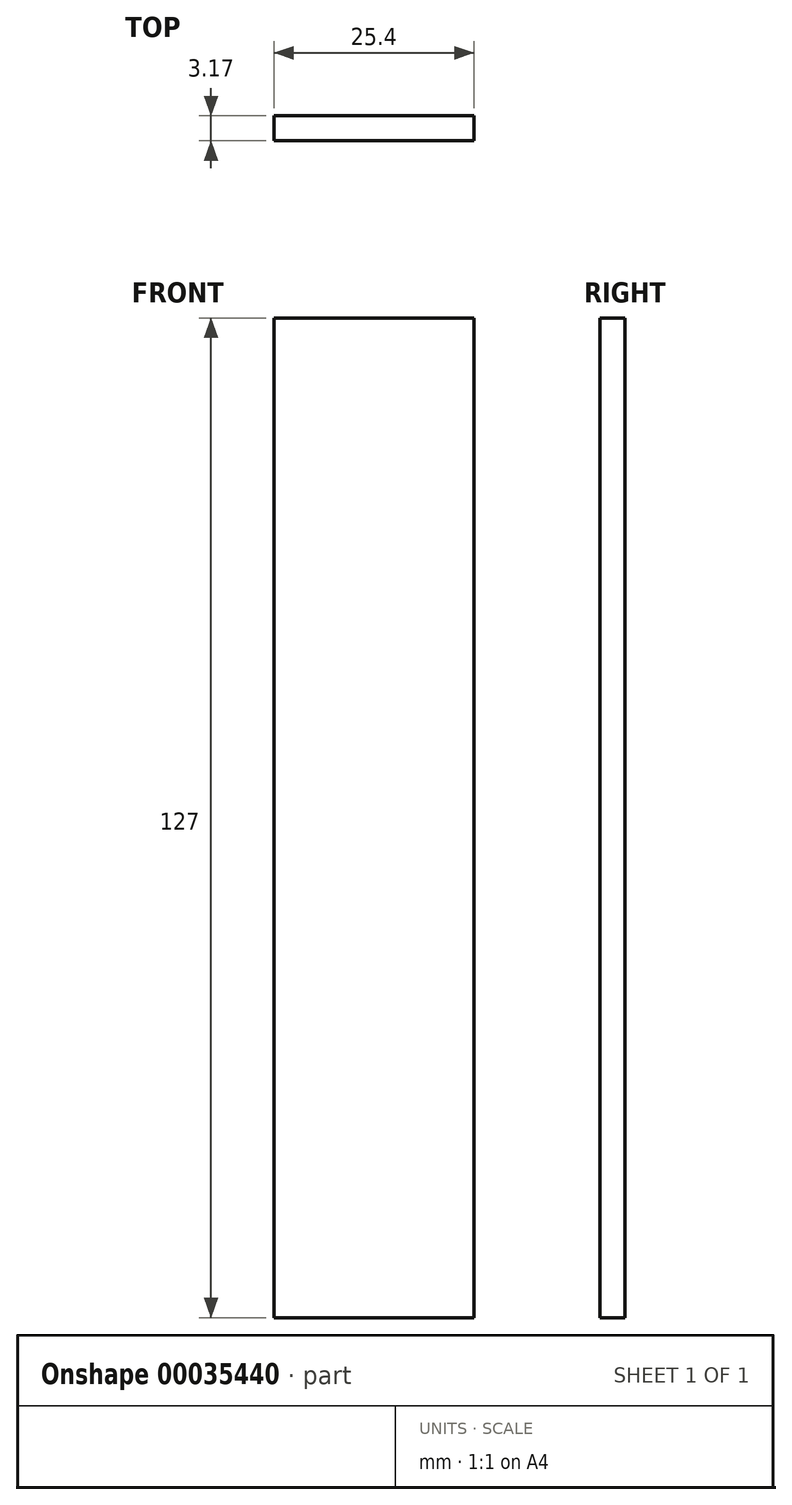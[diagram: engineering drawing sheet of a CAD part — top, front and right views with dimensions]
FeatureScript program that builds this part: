
annotation { "Feature Type Name" : "Feature", "Feature Type Description" : "" }
export const myFeature = defineFeature(function(context is Context, id is Id, definition is map)
    precondition{}
    {
        {
            var Q0;
            Q0=qCreatedBy(makeId("Front.planeOp"),FACE);
            var sketch = newSketch(context, id + "F0", { "sketchPlane" : qUnion([Q0])});
            skLineSegment(sketch, "E0.rect.bottom", {"start": v(12.7, 63.5) * mm, "end": v(-12.7, 63.5) * mm});
            skLineSegment(sketch, "E0.rect.top", {"start": v(12.7, -63.5) * mm, "end": v(-12.7, -63.5) * mm});
            skLineSegment(sketch, "E0.rect.left", {"start": v(12.7, 63.5) * mm, "end": v(12.7, -63.5) * mm});
            skLineSegment(sketch, "E0.rect.right", {"start": v(-12.7, 63.5) * mm, "end": v(-12.7, -63.5) * mm});
            skPoint(sketch, "E0.rect.middle", {"position": v(0, 0) * mm});
            skSolve(sketch);
        }
        {
            var Q0;
            Q0=makeQuery(id+"F0.imprint","IMPRINT",FACE,{"disambiguationData":[TD([[makeQuery(id+"F0.imprint","IMPRINT",EDGE,{"derivedFrom":sQuery(id+"F0.wireOp",EDGE,"E0.rect.bottom")}),1.0]])]});
            extrude(context, id + "F1", {"entities" : qUnion([Q0]), "depth" : 3.17 * mm});
        }
    });
